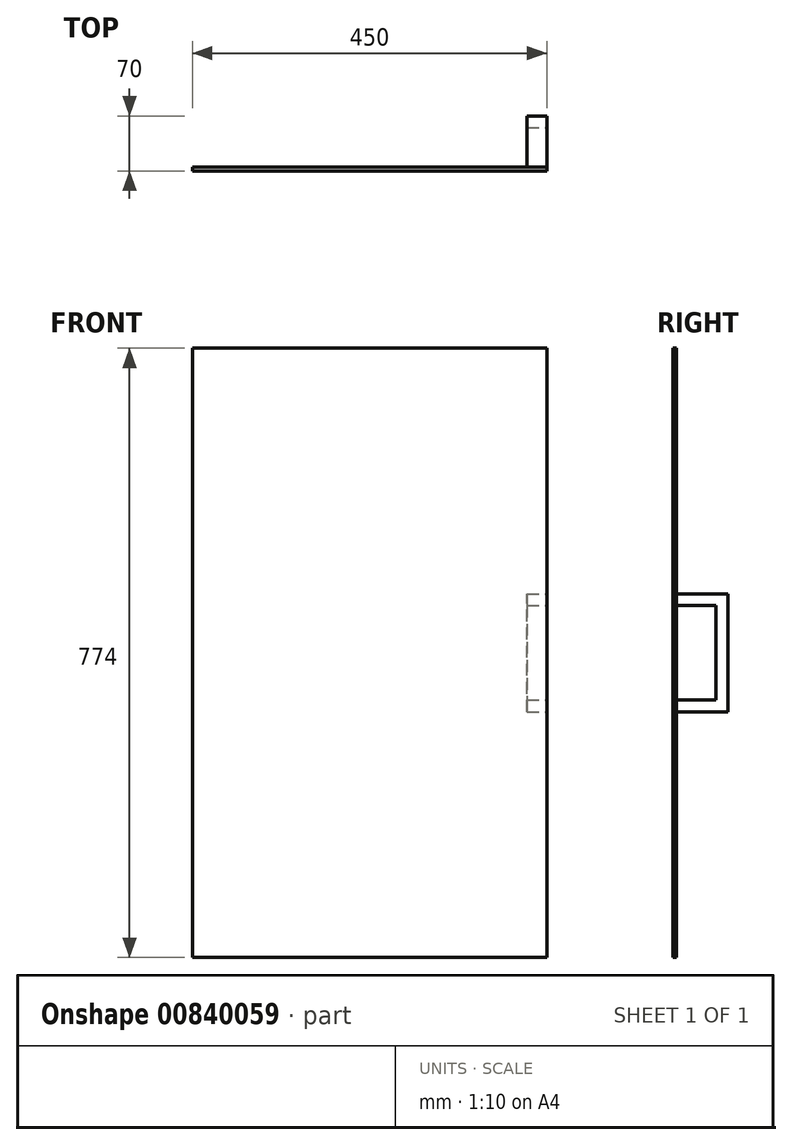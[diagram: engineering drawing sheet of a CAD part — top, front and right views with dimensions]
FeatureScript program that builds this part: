
annotation { "Feature Type Name" : "Feature", "Feature Type Description" : "" }
export const myFeature = defineFeature(function(context is Context, id is Id, definition is map)
    precondition{}
    {
        {
            var Q0;
            Q0=qCreatedBy(makeId("Front.planeOp"),FACE);
            var sketch = newSketch(context, id + "F0", { "sketchPlane" : qUnion([Q0])});
            skLineSegment(sketch, "E0.bottom", {"start": v(-240, 387) * mm, "end": v(210, 387) * mm});
            skLineSegment(sketch, "E0.top", {"start": v(-240, -387) * mm, "end": v(210, -387) * mm});
            skLineSegment(sketch, "E0.left", {"start": v(-240, 387) * mm, "end": v(-240, -387) * mm});
            skLineSegment(sketch, "E0.right", {"start": v(210, 387) * mm, "end": v(210, -387) * mm});
            skSolve(sketch);
        }
        {
            var Q0;
            Q0=makeQuery(id+"F0.imprint","IMPRINT",FACE,{"disambiguationData":[TD([[makeQuery(id+"F0.imprint","IMPRINT",EDGE,{"derivedFrom":sQuery(id+"F0.wireOp",EDGE,"E0.bottom")}),-1.0]])]});
            extrude(context, id + "F1", {"entities" : qUnion([Q0]), "endBound" : BoundingType.SYMMETRIC, "depth" : 5 * mm, "offsetDistance" : 25 * mm});
        }
        {
            var Q0;
            Q0=makeQuery(id+"F1.opExtrude","SWEPT_FACE",FACE,{"disambiguationData":[OSD([sQuery(id+"F0.wireOp",EDGE,"E0.right")])]});
            var sketch = newSketch(context, id + "F2", { "sketchPlane" : qUnion([Q0])});
            skLineSegment(sketch, "E1", {"start": v(2.5, 60) * mm, "end": v(52.5, 60) * mm});
            skLineSegment(sketch, "E2", {"start": v(52.5, 60) * mm, "end": v(52.5, 0) * mm});
            skLineSegment(sketch, "E3", {"start": v(2.5, 60) * mm, "end": v(2.5, 75) * mm});
            skLineSegment(sketch, "E4", {"start": v(2.5, 75) * mm, "end": v(67.5, 75) * mm});
            skLineSegment(sketch, "E5", {"start": v(67.5, 75) * mm, "end": v(67.5, 0) * mm});
            skLineSegment(sketch, "E6.MirrorCS", {"start": v(52.5, -60) * mm, "end": v(52.5, 0) * mm});
            skLineSegment(sketch, "E7.MirrorCS", {"start": v(67.5, -75) * mm, "end": v(67.5, 0) * mm});
            skLineSegment(sketch, "E8.MirrorCS", {"start": v(2.5, -75) * mm, "end": v(67.5, -75) * mm});
            skLineSegment(sketch, "E9.MirrorCS", {"start": v(2.5, -60) * mm, "end": v(52.5, -60) * mm});
            skLineSegment(sketch, "E10.MirrorCS", {"start": v(2.5, -60) * mm, "end": v(2.5, -75) * mm});
            skSolve(sketch);
        }
        {
            var Q0;
            Q0=makeQuery(id+"F2.imprint","IMPRINT",FACE,{"disambiguationData":[TD([[makeQuery(id+"F2.imprint","IMPRINT",EDGE,{"derivedFrom":sQuery(id+"F2.wireOp",EDGE,"E1")}),1.0]])]});
            extrude(context, id + "F3", {"entities" : qUnion([Q0]), "oppositeDirection" : true, "depth" : 25 * mm, "offsetDistance" : 25 * mm});
        }
    });
